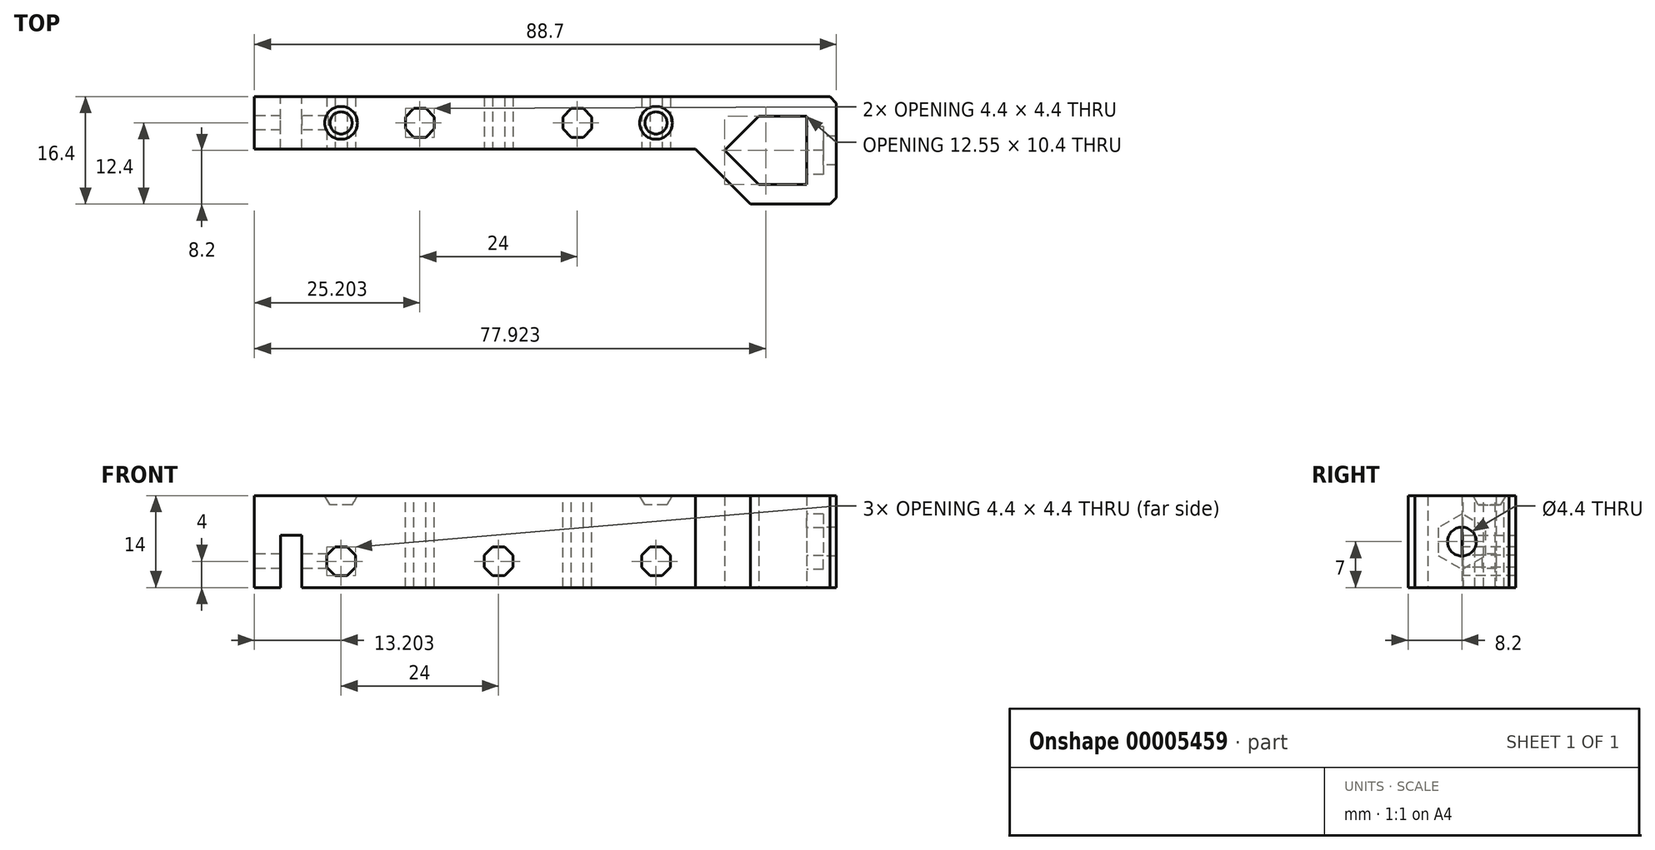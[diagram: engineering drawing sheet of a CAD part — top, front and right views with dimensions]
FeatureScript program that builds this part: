
annotation { "Feature Type Name" : "Feature", "Feature Type Description" : "" }
export const myFeature = defineFeature(function(context is Context, id is Id, definition is map)
    precondition{}
    {
        {
            var Q0;
            Q0=qCreatedBy(makeId("Top.planeOp"),FACE);
            var sketch = newSketch(context, id + "F0", { "sketchPlane" : qUnion([Q0]), "disableImprinting" : false});
            skCircle(sketch, "E0", {"center": v(0, 0) * mm, "radius": 5.2 * mm, "construction": true});
            skLineSegment(sketch, "E1", {"start": v(-7.35, 0) * mm, "end": v(-2.15, 5.2) * mm});
            skLineSegment(sketch, "E2", {"start": v(-2.15, 5.2) * mm, "end": v(5.2, 5.2) * mm});
            skLineSegment(sketch, "E3", {"start": v(5.2, 5.2) * mm, "end": v(5.2, -5.2) * mm});
            skLineSegment(sketch, "E4", {"start": v(5.2, -5.2) * mm, "end": v(-2.15, -5.2) * mm});
            skLineSegment(sketch, "E5", {"start": v(-2.15, -5.2) * mm, "end": v(-7.35, 0) * mm});
            skPoint(sketch, "E6", {"position": v(5.2, 0) * mm});
            skLineSegment(sketch, "E7", {"start": v(9.7, -8.2) * mm, "end": v(9.7, 8.2) * mm});
            skLineSegment(sketch, "E8", {"start": v(9.7, 8.2) * mm, "end": v(-71.8, 8.2) * mm});
            skLineSegment(sketch, "E9", {"start": v(-71.8, 8.2) * mm, "end": v(-71.8, 0.2) * mm});
            skLineSegment(sketch, "E10", {"start": v(-71.8, 0.2) * mm, "end": v(-11.8, 0.2) * mm});
            skLineSegment(sketch, "E11", {"start": v(-11.8, 0.2) * mm, "end": v(-3.4, -8.2) * mm});
            skLineSegment(sketch, "E12", {"start": v(-3.4, -8.2) * mm, "end": v(9.7, -8.2) * mm});
            skPoint(sketch, "E13", {"position": v(9.7, 0) * mm});
            skSolve(sketch);
        }
        {
            var Q0;
            Q0=makeQuery(id+"F0.imprint","IMPRINT",FACE,{"disambiguationData":[TD([[makeQuery(id+"F0.imprint","IMPRINT",EDGE,{"derivedFrom":sQuery(id+"F0.wireOp",EDGE,"E1")}),1.0]])]});
            extrude(context, id + "F1", {"entities" : qUnion([Q0]), "offsetDistance" : 25 * mm, "depth" : 14 * mm});
        }
        {
            var Q0;
            Q0=makeQuery(id+"F1.opExtrude","SWEPT_FACE",FACE,{"disambiguationData":[OSD([sQuery(id+"F0.wireOp",EDGE,"E3")])]});
            var sketch = newSketch(context, id + "F2", { "sketchPlane" : qUnion([Q0])});
            skCircle(sketch, "E14", {"center": v(0, 7) * mm, "radius": 2.2 * mm});
            skPoint(sketch, "E14.centerSnap0", {"position": v(-5.2, 7) * mm});
            skPoint(sketch, "E14.centerSnap1", {"position": v(0, 14) * mm});
            skCircle(sketch, "E15.cCircle", {"center": v(0, 7) * mm, "radius": 3.65 * mm, "construction": true});
            skLineSegment(sketch, "E15.0", {"start": v(3.65, 9.1) * mm, "end": v(3.65, 4.9) * mm});
            skLineSegment(sketch, "E15.1", {"start": v(3.65, 4.9) * mm, "end": v(0, 2.79) * mm});
            skLineSegment(sketch, "E15.2", {"start": v(0, 2.79) * mm, "end": v(-3.65, 4.9) * mm});
            skLineSegment(sketch, "E15.3", {"start": v(-3.65, 4.9) * mm, "end": v(-3.65, 9.1) * mm});
            skLineSegment(sketch, "E15.4", {"start": v(-3.65, 9.1) * mm, "end": v(0, 11.21) * mm});
            skLineSegment(sketch, "E15.5", {"start": v(0, 11.21) * mm, "end": v(3.65, 9.1) * mm});
            skPoint(sketch, "E15.0.midPoint", {"position": v(3.65, 7) * mm});
            skSolve(sketch);
        }
        {
            var Q0;
            Q0=makeQuery(id+"F2.imprint","IMPRINT",FACE,{"disambiguationData":[TD([[makeQuery(id+"F2.imprint","IMPRINT",EDGE,{"derivedFrom":sQuery(id+"F2.wireOp",EDGE,"E14")}),1.0]])]});
            extrude(context, id + "F3", {"entities" : qUnion([Q0]), "operationType" : NewBodyOperationType.REMOVE, "endBound" : BoundingType.THROUGH_ALL, "oppositeDirection" : true, "depth" : 25 * mm});
        }
        {
            var Q0;
            Q0=makeQuery(id+"F2.imprint","IMPRINT",FACE,{"disambiguationData":[TD([[makeQuery(id+"F2.imprint","IMPRINT",EDGE,{"derivedFrom":sQuery(id+"F2.wireOp",EDGE,"E14")}),-1.0]])]});
            extrude(context, id + "F4", {"entities" : qUnion([Q0]), "operationType" : NewBodyOperationType.REMOVE, "oppositeDirection" : true, "depth" : 2.5 * mm});
        }
        {
            var Q0;
            Q0=makeQuery(id+"F1.opExtrude","CAP_FACE",FACE,{"disambiguationData":[OSD([sQuery(id+"F0.wireOp",EDGE,"E1"),sQuery(id+"F0.wireOp",EDGE,"E2"),sQuery(id+"F0.wireOp",EDGE,"E3"),sQuery(id+"F0.wireOp",EDGE,"E4"),sQuery(id+"F0.wireOp",EDGE,"E5"),sQuery(id+"F0.wireOp",EDGE,"E7"),sQuery(id+"F0.wireOp",EDGE,"E8"),sQuery(id+"F0.wireOp",EDGE,"E9"),sQuery(id+"F0.wireOp",EDGE,"E10"),sQuery(id+"F0.wireOp",EDGE,"E11"),sQuery(id+"F0.wireOp",EDGE,"E12")])],"isStart":false});
            var sketch = newSketch(context, id + "F5", { "sketchPlane" : qUnion([Q0])});
            skCircle(sketch, "E16", {"center": v(-65.8, 4.2) * mm, "radius": 2.5 * mm});
            skPoint(sketch, "E16.centerSnap0", {"position": v(-71.8, 4.2) * mm});
            skCircle(sketch, "E17", {"center": v(-17.8, 4.2) * mm, "radius": 2.5 * mm});
            skLineSegment(sketch, "E18", {"start": v(-65.8, 4.2) * mm, "end": v(-17.8, 4.2) * mm, "construction": true});
            skPoint(sketch, "E19", {"position": v(-41.8, 4.2) * mm});
            skSolve(sketch);
        }
        {
            var Q0;
            Q0=makeQuery(id+"F5.imprint","IMPRINT",FACE,{"disambiguationData":[TD([[makeQuery(id+"F5.imprint","IMPRINT",EDGE,{"derivedFrom":sQuery(id+"F5.wireOp",EDGE,"E17")}),1.0]])]});
            var Q1;
            Q1=makeQuery(id+"F5.imprint","IMPRINT",FACE,{"disambiguationData":[TD([[makeQuery(id+"F5.imprint","IMPRINT",EDGE,{"derivedFrom":sQuery(id+"F5.wireOp",EDGE,"E16")}),1.0]])]});
            extrude(context, id + "F6", {"entities" : qUnion([Q0, Q1]), "operationType" : NewBodyOperationType.REMOVE, "oppositeDirection" : true, "depth" : 1.4 * mm, "hasDraft" : true, "draftAngle" : 30 * degree, "draftPullDirection" : true});
        }
        {
            var Q0;
            Q0=makeQuery(id+"F1.opExtrude","SWEPT_FACE",FACE,{"disambiguationData":[OSD([sQuery(id+"F0.wireOp",EDGE,"E10")])]});
            var sketch = newSketch(context, id + "F7", { "sketchPlane" : qUnion([Q0])});
            skLineSegment(sketch, "E20", {"start": v(-41.8, 0) * mm, "end": v(-41.8, 14) * mm, "construction": true});
            skCircle(sketch, "E21.cCircle", {"center": v(-65.8, 4) * mm, "radius": 2.2 * mm, "construction": true});
            skLineSegment(sketch, "E21.0", {"start": v(-63.6, 4.91) * mm, "end": v(-63.6, 3.09) * mm});
            skLineSegment(sketch, "E21.1", {"start": v(-63.6, 3.09) * mm, "end": v(-64.89, 1.8) * mm});
            skLineSegment(sketch, "E21.2", {"start": v(-64.89, 1.8) * mm, "end": v(-66.7, 1.8) * mm});
            skLineSegment(sketch, "E21.3", {"start": v(-66.7, 1.8) * mm, "end": v(-68, 3.09) * mm});
            skLineSegment(sketch, "E21.4", {"start": v(-68, 3.09) * mm, "end": v(-68, 4.91) * mm});
            skLineSegment(sketch, "E21.5", {"start": v(-68, 4.91) * mm, "end": v(-66.7, 6.2) * mm});
            skLineSegment(sketch, "E21.6", {"start": v(-66.7, 6.2) * mm, "end": v(-64.89, 6.2) * mm});
            skLineSegment(sketch, "E21.7", {"start": v(-64.89, 6.2) * mm, "end": v(-63.6, 4.91) * mm});
            skPoint(sketch, "E21.0.midPoint", {"position": v(-63.6, 4) * mm});
            skCircle(sketch, "E22.cCircle", {"center": v(-41.8, 4) * mm, "radius": 2.2 * mm, "construction": true});
            skLineSegment(sketch, "E22.0", {"start": v(-39.6, 4.91) * mm, "end": v(-39.6, 3.09) * mm});
            skLineSegment(sketch, "E22.1", {"start": v(-39.6, 3.09) * mm, "end": v(-40.89, 1.8) * mm});
            skLineSegment(sketch, "E22.2", {"start": v(-40.89, 1.8) * mm, "end": v(-42.7, 1.8) * mm});
            skLineSegment(sketch, "E22.3", {"start": v(-42.7, 1.8) * mm, "end": v(-44, 3.09) * mm});
            skLineSegment(sketch, "E22.4", {"start": v(-44, 3.09) * mm, "end": v(-44, 4.91) * mm});
            skLineSegment(sketch, "E22.5", {"start": v(-44, 4.91) * mm, "end": v(-42.7, 6.2) * mm});
            skLineSegment(sketch, "E22.6", {"start": v(-42.7, 6.2) * mm, "end": v(-40.89, 6.2) * mm});
            skLineSegment(sketch, "E22.7", {"start": v(-40.89, 6.2) * mm, "end": v(-39.6, 4.91) * mm});
            skPoint(sketch, "E22.0.midPoint", {"position": v(-39.6, 4) * mm});
            skCircle(sketch, "E23.cCircle", {"center": v(-17.8, 4) * mm, "radius": 2.2 * mm, "construction": true});
            skLineSegment(sketch, "E23.0", {"start": v(-15.6, 4.91) * mm, "end": v(-15.6, 3.09) * mm});
            skLineSegment(sketch, "E23.1", {"start": v(-15.6, 3.09) * mm, "end": v(-16.89, 1.8) * mm});
            skLineSegment(sketch, "E23.2", {"start": v(-16.89, 1.8) * mm, "end": v(-18.7, 1.8) * mm});
            skLineSegment(sketch, "E23.3", {"start": v(-18.7, 1.8) * mm, "end": v(-20, 3.09) * mm});
            skLineSegment(sketch, "E23.4", {"start": v(-20, 3.09) * mm, "end": v(-20, 4.91) * mm});
            skLineSegment(sketch, "E23.5", {"start": v(-20, 4.91) * mm, "end": v(-18.7, 6.2) * mm});
            skLineSegment(sketch, "E23.6", {"start": v(-18.7, 6.2) * mm, "end": v(-16.89, 6.2) * mm});
            skLineSegment(sketch, "E23.7", {"start": v(-16.89, 6.2) * mm, "end": v(-15.6, 4.91) * mm});
            skPoint(sketch, "E23.0.midPoint", {"position": v(-15.6, 4) * mm});
            skSolve(sketch);
        }
        {
            var Q0;
            Q0 = qSketchRegion(id + "F7", true);
            extrude(context, id + "F8", {"entities" : qUnion([Q0]), "operationType" : NewBodyOperationType.REMOVE, "endBound" : BoundingType.THROUGH_ALL, "oppositeDirection" : true, "depth" : 25 * mm});
        }
        {
            var Q0;
            Q0=makeQuery(id+"F1.opExtrude","CAP_FACE",FACE,{"disambiguationData":[OSD([sQuery(id+"F0.wireOp",EDGE,"E1"),sQuery(id+"F0.wireOp",EDGE,"E2"),sQuery(id+"F0.wireOp",EDGE,"E3"),sQuery(id+"F0.wireOp",EDGE,"E4"),sQuery(id+"F0.wireOp",EDGE,"E5"),sQuery(id+"F0.wireOp",EDGE,"E7"),sQuery(id+"F0.wireOp",EDGE,"E8"),sQuery(id+"F0.wireOp",EDGE,"E9"),sQuery(id+"F0.wireOp",EDGE,"E10"),sQuery(id+"F0.wireOp",EDGE,"E11"),sQuery(id+"F0.wireOp",EDGE,"E12")])],"isStart":false});
            var sketch = newSketch(context, id + "F9", { "sketchPlane" : qUnion([Q0])});
            skPoint(sketch, "E24.cCircle.centerSnap0", {"position": v(-71.8, 4.2) * mm});
            skLineSegment(sketch, "E25", {"start": v(-41.8, 0.2) * mm, "end": v(-41.8, 8.2) * mm, "construction": true});
            skCircle(sketch, "E26.cCircle", {"center": v(-53.8, 4.2) * mm, "radius": 2.2 * mm, "construction": true});
            skPoint(sketch, "E26.cCircle.centerSnap0", {"position": v(-41.8, 4.2) * mm});
            skLineSegment(sketch, "E26.0", {"start": v(-54.7, 6.4) * mm, "end": v(-52.89, 6.4) * mm});
            skLineSegment(sketch, "E26.1", {"start": v(-52.89, 6.4) * mm, "end": v(-51.6, 5.11) * mm});
            skLineSegment(sketch, "E26.2", {"start": v(-51.6, 5.11) * mm, "end": v(-51.6, 3.29) * mm});
            skLineSegment(sketch, "E26.3", {"start": v(-51.6, 3.29) * mm, "end": v(-52.89, 2) * mm});
            skLineSegment(sketch, "E26.4", {"start": v(-52.89, 2) * mm, "end": v(-54.7, 2) * mm});
            skLineSegment(sketch, "E26.5", {"start": v(-54.7, 2) * mm, "end": v(-56, 3.29) * mm});
            skLineSegment(sketch, "E26.6", {"start": v(-56, 3.29) * mm, "end": v(-56, 5.11) * mm});
            skLineSegment(sketch, "E26.7", {"start": v(-56, 5.11) * mm, "end": v(-54.7, 6.4) * mm});
            skPoint(sketch, "E26.0.midPoint", {"position": v(-53.8, 6.4) * mm});
            skLineSegment(sketch, "E27.MirrorCS", {"start": v(-27.6, 5.11) * mm, "end": v(-28.89, 6.4) * mm});
            skLineSegment(sketch, "E28.MirrorCS", {"start": v(-28.89, 2) * mm, "end": v(-27.6, 3.29) * mm});
            skLineSegment(sketch, "E29.MirrorCS", {"start": v(-28.89, 6.4) * mm, "end": v(-30.7, 6.4) * mm});
            skLineSegment(sketch, "E30.MirrorCS", {"start": v(-32, 3.29) * mm, "end": v(-30.7, 2) * mm});
            skLineSegment(sketch, "E31.MirrorCS", {"start": v(-30.7, 6.4) * mm, "end": v(-32, 5.11) * mm});
            skLineSegment(sketch, "E32.MirrorCS", {"start": v(-30.7, 2) * mm, "end": v(-28.89, 2) * mm});
            skLineSegment(sketch, "E33.MirrorCS", {"start": v(-32, 5.11) * mm, "end": v(-32, 3.29) * mm});
            skLineSegment(sketch, "E34.MirrorCS", {"start": v(-27.6, 3.29) * mm, "end": v(-27.6, 5.11) * mm});
            skCircle(sketch, "E35.MirrorC", {"center": v(-29.8, 4.2) * mm, "radius": 2.2 * mm, "construction": true});
            skPoint(sketch, "E36.MirrorP", {"position": v(-29.8, 6.4) * mm});
            skSolve(sketch);
        }
        {
            var Q0;
            Q0 = qSketchRegion(id + "F9", true);
            extrude(context, id + "F10", {"entities" : qUnion([Q0]), "operationType" : NewBodyOperationType.REMOVE, "endBound" : BoundingType.THROUGH_ALL, "oppositeDirection" : true, "depth" : 25 * mm});
        }
        {
            var Q0;
            Q0=makeQuery(id+"F1.opExtrude","SWEPT_EDGE",EDGE,{"disambiguationData":[OSD([sQuery(id+"F0.wireOp",EDGE,"E7"),sQuery(id+"F0.wireOp",EDGE,"E12")])]});
            var Q1;
            Q1=makeQuery(id+"F1.opExtrude","SWEPT_EDGE",EDGE,{"disambiguationData":[OSD([sQuery(id+"F0.wireOp",EDGE,"E7"),sQuery(id+"F0.wireOp",EDGE,"E8")])]});
            chamfer(context, id + "F11", {"entities" : qUnion([Q0, Q1]), "width" : 1 * mm, "tangentPropagation" : true});
        }
        {
            var Q0;
            Q0=makeQuery(id+"F1.opExtrude","CAP_FACE",FACE,{"disambiguationData":[OSD([sQuery(id+"F0.wireOp",EDGE,"E1"),sQuery(id+"F0.wireOp",EDGE,"E2"),sQuery(id+"F0.wireOp",EDGE,"E3"),sQuery(id+"F0.wireOp",EDGE,"E4"),sQuery(id+"F0.wireOp",EDGE,"E5"),sQuery(id+"F0.wireOp",EDGE,"E7"),sQuery(id+"F0.wireOp",EDGE,"E8"),sQuery(id+"F0.wireOp",EDGE,"E9"),sQuery(id+"F0.wireOp",EDGE,"E10"),sQuery(id+"F0.wireOp",EDGE,"E11"),sQuery(id+"F0.wireOp",EDGE,"E12")])],"isStart":false});
            var sketch = newSketch(context, id + "F12", { "sketchPlane" : qUnion([Q0])});
            skCircle(sketch, "E37", {"center": v(-0.99, 0) * mm, "radius": 4.5 * mm, "construction": true});
            skSolve(sketch);
        }
        {
            var Q0;
            Q0=makeQuery(id+"F1.opExtrude","SWEPT_FACE",FACE,{"disambiguationData":[OSD([sQuery(id+"F0.wireOp",EDGE,"E8")])]});
            var sketch = newSketch(context, id + "F13", { "sketchPlane" : qUnion([Q0])});
            skLineSegment(sketch, "E38", {"start": v(71.8, 14) * mm, "end": v(79, 14) * mm});
            skLineSegment(sketch, "E39", {"start": v(79, 14) * mm, "end": v(79, 0) * mm});
            skLineSegment(sketch, "E40", {"start": v(79, 0) * mm, "end": v(75, 0) * mm});
            skLineSegment(sketch, "E41", {"start": v(75, 0) * mm, "end": v(75, 8) * mm});
            skLineSegment(sketch, "E42", {"start": v(75, 8) * mm, "end": v(71.8, 8) * mm});
            skLineSegment(sketch, "E43", {"start": v(71.8, 14) * mm, "end": v(71.8, 8) * mm});
            skSolve(sketch);
        }
        {
            var Q0;
            Q0 = qSketchRegion(id + "F13", true);
            var Q1;
            Q1=makeQuery(id+"F1.opExtrude","SWEPT_FACE",FACE,{"disambiguationData":[OSD([sQuery(id+"F0.wireOp",EDGE,"E10")])]});
            extrude(context, id + "F14", {"entities" : qUnion([Q0]), "operationType" : NewBodyOperationType.ADD, "endBound" : BoundingType.UP_TO_SURFACE, "oppositeDirection" : true, "depth" : 25 * mm, "endBoundEntityFace" : qUnion([Q1]), "offsetDistance" : 25 * mm});
        }
        {
            var Q0;
            Q0=makeQuery(id+"F14.opExtrude","SWEPT_FACE",FACE,{"disambiguationData":[OSD([sQuery(id+"F13.wireOp",EDGE,"E39")])]});
            var sketch = newSketch(context, id + "F15", { "sketchPlane" : qUnion([Q0])});
            skLineSegment(sketch, "E44.0.0", {"start": v(-8.2, 3.09) * mm, "end": v(-8.2, 4.91) * mm, "construction": true});
            skLineSegment(sketch, "E44.0.1", {"start": v(-8.2, 4.91) * mm, "end": v(-0.2, 4.91) * mm, "construction": true});
            skLineSegment(sketch, "E44.0.2", {"start": v(-0.2, 4.91) * mm, "end": v(-0.2, 3.09) * mm, "construction": true});
            skLineSegment(sketch, "E44.0.3", {"start": v(-0.2, 3.09) * mm, "end": v(-8.2, 3.09) * mm, "construction": true});
            skLineSegment(sketch, "E45.bottom", {"start": v(-3.1, 5.1) * mm, "end": v(-5.3, 5.1) * mm});
            skLineSegment(sketch, "E45.top", {"start": v(-3.1, 2.9) * mm, "end": v(-5.3, 2.9) * mm});
            skLineSegment(sketch, "E45.left", {"start": v(-3.1, 5.1) * mm, "end": v(-3.1, 2.9) * mm});
            skLineSegment(sketch, "E45.right", {"start": v(-5.3, 5.1) * mm, "end": v(-5.3, 2.9) * mm});
            skPoint(sketch, "E45.middle", {"position": v(-4.2, 4) * mm});
            skPoint(sketch, "E45.middle.positionSnap0", {"position": v(-4.2, 4.91) * mm});
            skPoint(sketch, "E45.middle.positionSnap1", {"position": v(-8.2, 4) * mm});
            skPoint(sketch, "E45.centerSnap0", {"position": v(-4.2, 4.91) * mm});
            skPoint(sketch, "E45.centerSnap1", {"position": v(-8.2, 4) * mm});
            skSolve(sketch);
        }
        {
            var Q0;
            Q0=makeQuery(id+"F15.imprint","IMPRINT",FACE,{"disambiguationData":[TD([[makeQuery(id+"F15.imprint","IMPRINT",EDGE,{"derivedFrom":sQuery(id+"F15.wireOp",EDGE,"E45.bottom")}),1.0]])]});
            extrude(context, id + "F16", {"entities" : qUnion([Q0]), "operationType" : NewBodyOperationType.REMOVE, "oppositeDirection" : true, "depth" : 12.4 * mm, "offsetDistance" : 25 * mm});
        }
    });
